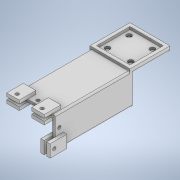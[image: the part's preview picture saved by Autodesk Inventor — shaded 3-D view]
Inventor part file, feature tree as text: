
AUTODESK INVENTOR PART (.ipt)
format: ipt  version: 2020 (Build 240168000, 168)  size: 320,512 bytes
history: native  units: in
note: dims shown in document units (in); Inventor stores cm internally (conversion verified against a paired STEP export)
features: sketch x14, extrude x13, mirror x3, fillet x1
ambient origin geometry x8: Origin, YZ Plane, XZ Plane, XY Plane, X Axis, Y Axis, Z Axis, Center Point
bodies: Solid1 (feature_tree)
feature tree (31):
  extrude  "Extrusion1"  Depth=1.8898in
  extrude  "Extrusion2"  Depth=0.1575in
  mirror  "Mirror1"
  extrude  "Extrusion3"  Depth=0.1575in
  extrude  "Extrusion4"  Depth=0.1575in
  extrude  "Extrusion5"  Depth=0.1181in
  extrude  "Extrusion6"  Depth=0.1181in
  mirror  "Mirror2"
  extrude  "Extrusion7"  Depth=0.1575in
  mirror  "Mirror3"
  extrude  "Extrusion12"  Depth=0.1575in
  extrude  "Extrusion13"  Depth=0.1575in
  sketch  "Sketch14"  dims[d23=0.1575in d24=0.0in d25=0.2362in]
  extrude  "Extrusion14"  Depth=0.2362in
  extrude  "Extrusion15"  Depth=0.2362in
  extrude  "Extrusion16"  Depth=0.1575in TaperAngle=0.0deg
  extrude  "Extrusion17"  Depth=0.5906in
  fillet  "Fillet1"  Radius=0.7874in
  sketch  "Sketch1"  dims[d0=1.8898in d1=10.8661in]
  sketch  "Sketch2"  dims[d2=0.1181in d3=0.0in d4=0.1575in]
  sketch  "Sketch3"  dims[d5=1.8898in d6=0.1575in]
  sketch  "Sketch4"  dims[d7=0.1575in d8=0.1575in]
  sketch  "Sketch5"  dims[d9=0.1181in d10=0.0in d11=0.1181in]
  sketch  "Sketch6"  dims[d12=0.1181in d13=0.1181in]
  sketch  "Sketch7"  dims[d14=1.378in d15=0.0in d16=0.1575in]
  sketch  "Sketch12"  dims[d17=0.315in d18=0.0in d19=0.1575in]
  sketch  "Sketch13"  dims[d20=0.1575in d21=0.0in d22=0.1575in]
  sketch  "Sketch15"  dims[d26=0.2362in d27=0.2362in]
  sketch  "Sketch16"  dims[d28=0.2362in d29=0.1575in d30=0.0in]
  sketch  "Sketch17"  dims[d53=3.937in d54=0.0in d55=0.5906in d56=0.7874in]
  sketch  "Sketch18"  dims[d57=0.5906in d58=0.7874in d59=0.1575in d60=0.2756in d61=0.0in d62=0.0in d63=0.7874in d64=0.5906in d65=0.1575in d66=0.2756in d67=0.0in d68=0.0in d69=0.1575in d70=0.1575in d71=0.1575in d72=0.7874in d73=0.0in d74=0.1575in d75=0.1575in d76=0.7874in d77=0.0in d78=0.3937in d79=0.0in d80=1.1024in d81=1.0236in d82=1.0236in d83=1.1024in d84=0.2756in d85=0.2756in d86=0.2756in d87=0.2362in d88=0.0787in]
